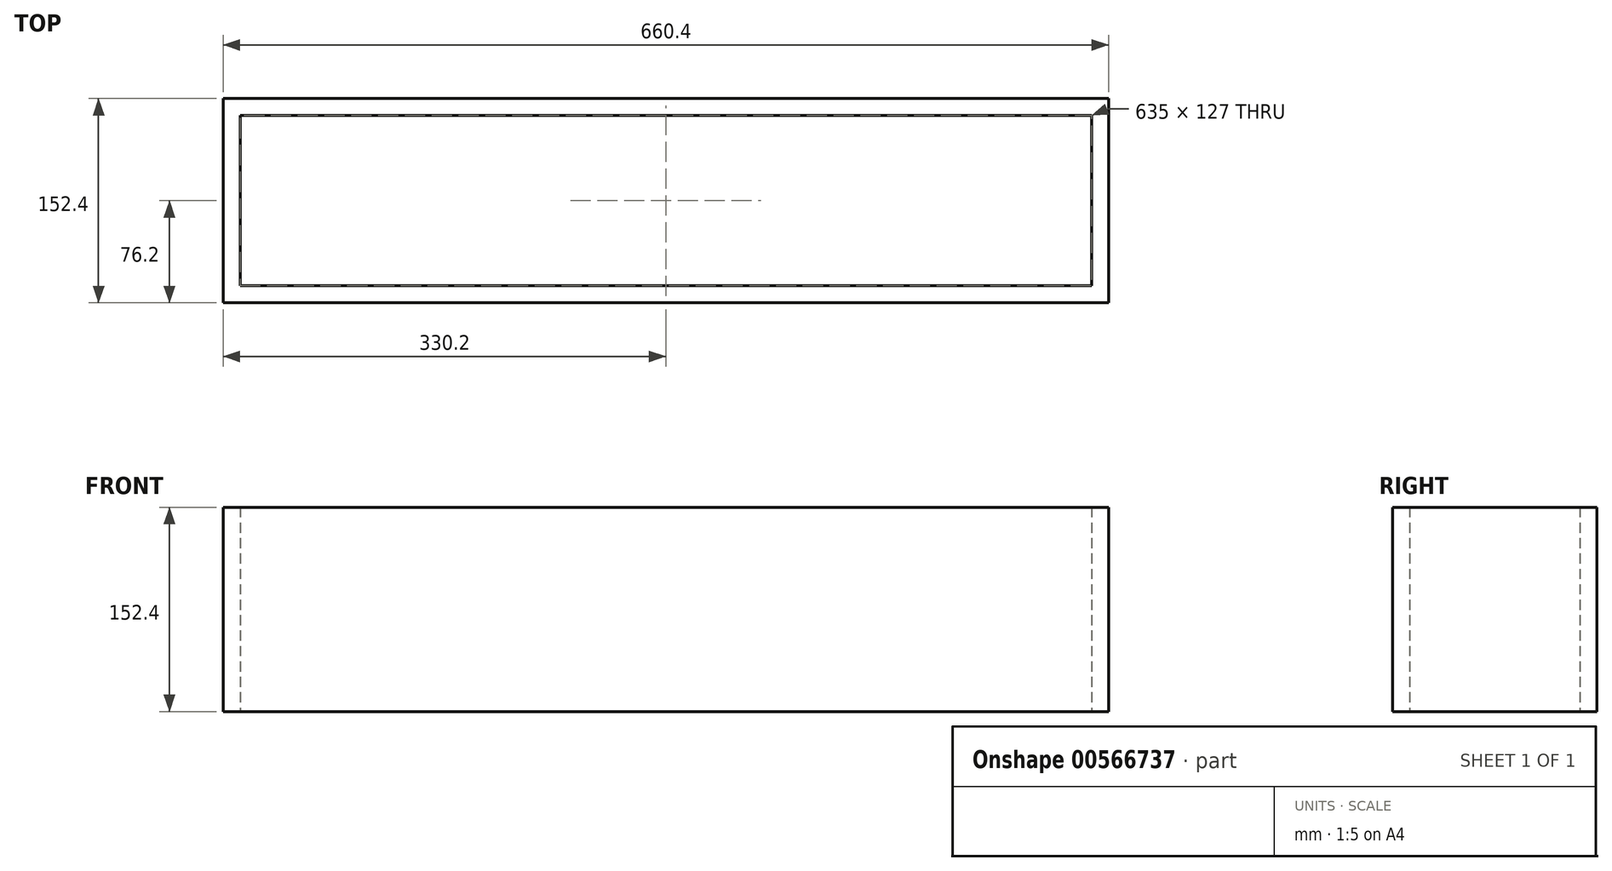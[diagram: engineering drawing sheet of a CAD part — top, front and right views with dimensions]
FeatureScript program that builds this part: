
annotation { "Feature Type Name" : "Feature", "Feature Type Description" : "" }
export const myFeature = defineFeature(function(context is Context, id is Id, definition is map)
    precondition{}
    {
        {
            var Q0;
            Q0=qCreatedBy(makeId("Top.planeOp"),FACE);
            var sketch = newSketch(context, id + "F0", { "sketchPlane" : qUnion([Q0])});
            skLineSegment(sketch, "E0.bottom", {"start": v(317.5, -63.5) * mm, "end": v(-317.5, -63.5) * mm});
            skLineSegment(sketch, "E0.top", {"start": v(317.5, 63.5) * mm, "end": v(-317.5, 63.5) * mm});
            skLineSegment(sketch, "E0.left", {"start": v(317.5, -63.5) * mm, "end": v(317.5, 63.5) * mm});
            skLineSegment(sketch, "E0.right", {"start": v(-317.5, -63.5) * mm, "end": v(-317.5, 63.5) * mm});
            skPoint(sketch, "E0.middle", {"position": v(0, 0) * mm});
            skLineSegment(sketch, "E1.bottom", {"start": v(330.2, -76.2) * mm, "end": v(-330.2, -76.2) * mm});
            skLineSegment(sketch, "E1.top", {"start": v(330.2, 76.2) * mm, "end": v(-330.2, 76.2) * mm});
            skLineSegment(sketch, "E1.left", {"start": v(330.2, -76.2) * mm, "end": v(330.2, 76.2) * mm});
            skLineSegment(sketch, "E1.right", {"start": v(-330.2, -76.2) * mm, "end": v(-330.2, 76.2) * mm});
            skSolve(sketch);
        }
        {
            var Q0;
            Q0=makeQuery(id+"F0.imprint","IMPRINT",FACE,{"disambiguationData":[TD([[makeQuery(id+"F0.imprint","IMPRINT",EDGE,{"derivedFrom":sQuery(id+"F0.wireOp",EDGE,"E0.bottom")}),1.0]])]});
            extrude(context, id + "F1", {"entities" : qUnion([Q0]), "depth" : 152.4 * mm, "offsetDistance" : 25.4 * mm});
        }
    });
